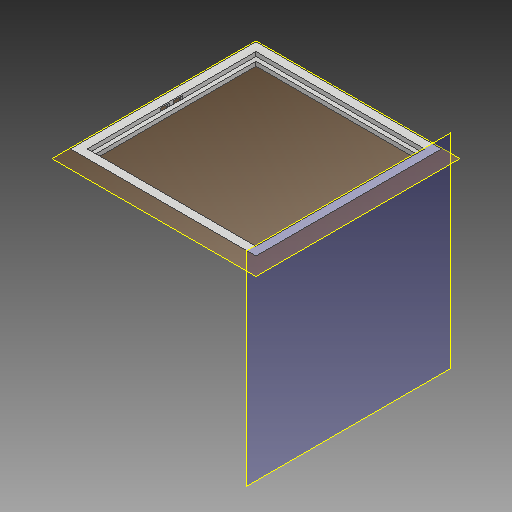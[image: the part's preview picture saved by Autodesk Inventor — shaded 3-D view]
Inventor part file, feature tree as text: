
AUTODESK INVENTOR PART (.ipt)
format: ipt  version: 2018.3 (Build 223284000, 284)  size: 173,568 bytes
history: native  units: mm
features: reference x19, other x10, extrude x4, sketch x4, plane x2, chamfer x1
ambient origin geometry x8: Origin, YZ Plane, XZ Plane, XY Plane, X Axis, Y Axis, Z Axis, Center Point
bodies: Volumenkörper1 (feature_tree)
feature tree (40):
  extrude  "Extrusion1"  Depth=20.0mm TaperAngle=45.0deg
  chamfer  "Fase1"  Distance=17.0mm
  plane  "Arbeitsebene1"
  extrude  "Extrusion2"  Depth=10.0mm
  extrude  "Extrusion3"  Depth=10.0mm
  plane  "Arbeitsebene3"
  extrude  "Extrusion4"  Depth=10.0mm TaperAngle=0.0deg
  sketch  "Skizze1"  dims[d0=20.0mm d1=0.0mm d2=20.0mm d3=2.0mm d4=45.0deg]
  reference  "Referenz1"
  reference  "Referenz2"
  reference  "Referenz3"
  reference  "Referenz4"
  reference  "Referenz5"
  sketch  "Skizze3"  dims[d5=-20.0mm d6=17.0mm d7=0.0mm]
  reference  "Referenz12"
  reference  "Referenz13"
  reference  "Referenz14"
  reference  "Referenz15"
  reference  "Referenz16"
  reference  "Referenz17"
  reference  "Referenz18"
  reference  "Referenz19"
  sketch  "Skizze5"  dims[d8=10.0mm d9=10.0mm]
  sketch  "Skizze6"  dims[d10=10.0mm d11=10.0mm d12=10.0mm d13=0.0mm d14=25.0mm d15=0.0mm]
  reference  "Referenz20"
  reference  "Referenz21"
  reference  "Referenz22"
  reference  "Referenz23"
  reference  "Referenz24"
  reference  "Referenz25"
  parser-record x1  (decoder bookkeeping rows leaked as tree rows — omitted from the tree; the rows remain in map.json)
  other  "SmartCube_Quadratisch.iam"
  other  "Wand2_MIR:1"
  other  "Wand1:1"
  other  "Wand1_MIR:1"
  other  "Wand2:1"
  other  "PV_Modul:1"
  other  "<userpath>\Documents\Dipl\Smartcube_Construction\Version_3\Baugruppe1.iam"
  other  "Baugruppe1.iam"
  other  "PV_Ramen_CPY_3_2:1"
note: 1 file-system path scrubbed to <path> (originals preserved in map.json)
